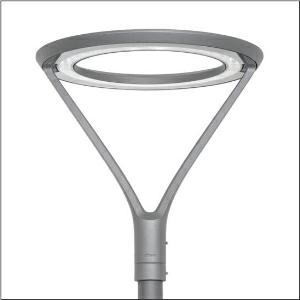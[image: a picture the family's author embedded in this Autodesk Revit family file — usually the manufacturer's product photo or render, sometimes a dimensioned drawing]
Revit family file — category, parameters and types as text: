
# Revit family: dl_r__20___pl1_2s_5xa51283ws008p_a586
name_source: partatom
category: Lighting Fixtures
units: mm (PartAtom-declared; Revit-internal decimal feet)

## family parameters
Cut with Voids When Loaded = No
Host = Face
Light Source = No
Part Type = Normal
Room Calculation Point = No
Round Connector Dimension = Use Diameter
Shared = No

## types (1)
- --- (1 x LED, 4250 lm, 34.3 W, 3000K)
    Apparent Load = 34 VA
    CIE Flux Codes = 33 78 99 100 100
    Color Rendering = 70
    Color Temperature = 3000K
    Default Elevation = 1800 mm
    Description = DL® 20, mast luminaire, primary light control with reflector, highly specular, primary optical cover: cover, of toughened safety glass of clear glass with excellent transmission level, light distribution: PL1.2s, light emission: direct distribution, primary light characteristic: symmetric, installation type: post-top, LED, High Power LED, rated luminous flux: 4.210lm, luminous efficacy: 80lm/W, light colour: 730, colour temperature: 3000K, control gear: ECG Plus, control: overheat protection, power reduction, digital communication interface, constant luminous flux control, time-dependent luminous flux control, flexible luminous flux parameterisation, electronic power reduction, mains connection: 230..240V, 50/60Hz, connection cable pre-assembled, cable length: 5m, start of lifetime: 53W, end of service life: 54W, reduction: 24W, luminaire housing, upper part, of cast aluminium, powder-coated, Siteco® metallic grey (DB 702S), diameter: 690mm, height: 690mm, spigot size: 76mm (post-top), luminaire housing, of cast aluminium, powder-coated, Siteco® metallic grey (DB 702S), equipment: Power, protection rating (complete): IP66, insulation class (complete): insulation class II (safety insulation), certification: CE, ENEC, VDE, impact resistance: IK08, permissible operating ambient temperature: -25..+30°C, standard-compliant lighting for roads and squares, packaging unit: 1 piece

Light Distribution: PL1.2s
    Height = 690 mm
    Lamp = 1 x LED
    Lamp Light Flux = 4250 lm
    Lamp Power = 34.3 W
    Lamp count = 1
    Length = 690 mm
    Luminous efficacy = 124 lm/W
    Manufacturer = Siteco
    ModVariant = No
    Model = 5XA51283WS008P
    Number of Poles = 1
    OnlyDefault = Yes
    Power Factor = 1
    Product Name = DL® 20 | PL1.2s
    Product group = mast luminaire | pylon top
    ProductGroupID = 6100
    Protection Class = Protection class II
    Protection Degree = IP 66
    RLX_Detail_Level = 1
    RLX_Emergency_Light_Flux = 0 lm
    RLX_Emergency_Type = 0
    RLX_Emergency_Type_DB = No
    RlxData = <blob elided: 204373 chars, md5=ec395621>
    Socket = socket
    Standby Power = 0 W
    System Light Flux = 4250 lm
    System Power = 34 W
    Type Comments = factory setting: luminous flux: 100 % | dim-lin: 254 | 464 mA
    Type Image = l_1006001.jpg
    URL = http://relux.com
    VarID = @adj_027981
    Voltage = 0 V
    Weight = 0.00 kg
    Width = 0 mm  [stored 0 ft]

note: [stored X ft] marks values corroborated as IEEE doubles in the binary element streams (Revit-internal decimal feet)

## geometry (parser evidence)
native form markers: Blend x4, Sweep x11
no freeform markers — native parametric forms only
